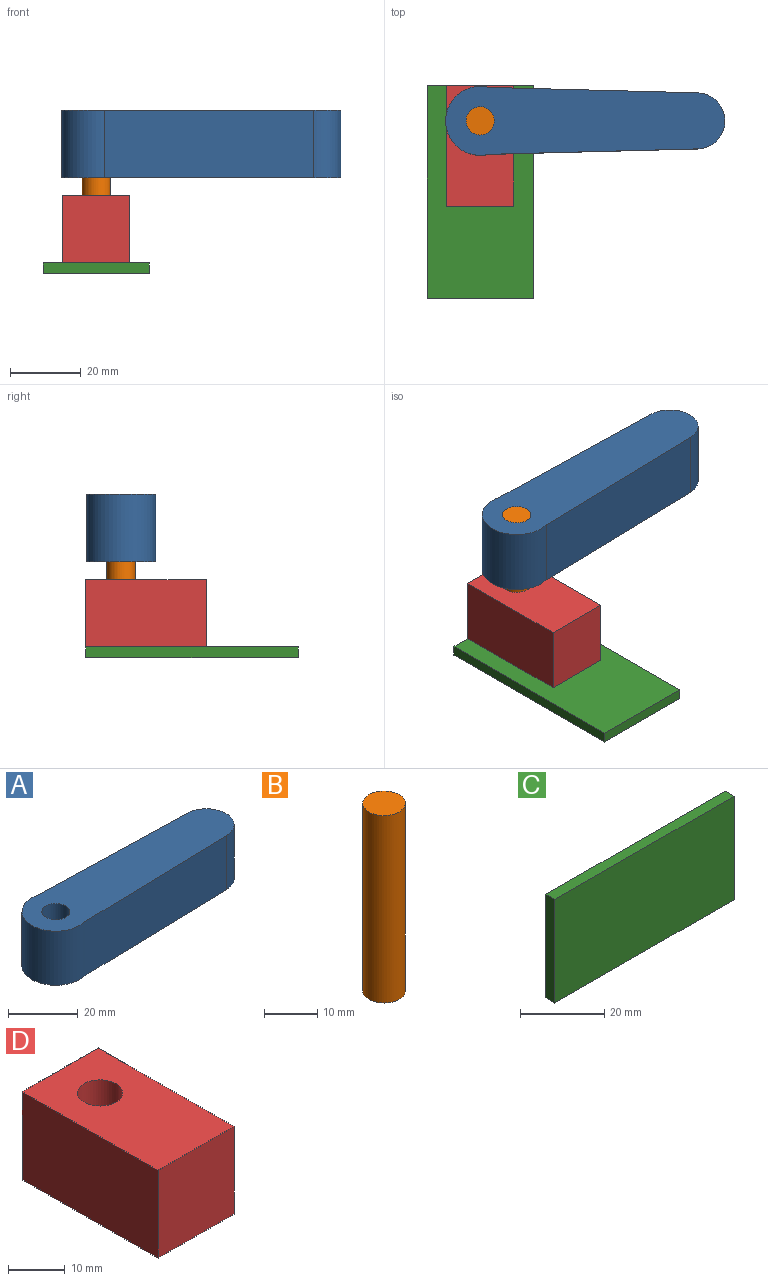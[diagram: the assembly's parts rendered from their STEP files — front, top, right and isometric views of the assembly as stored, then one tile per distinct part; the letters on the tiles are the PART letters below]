
ASSEMBLY  parts=4 mates=3
PART A: 7 faces, bbox 78.8x19.5x19 mm
  f0: cylinder r=7.91mm len=19mm, axis (0,0,-1), area 464.2mm2, adj f1,f3,f5,f6
  f1: plane 58.96x19mm, normal (0.03,1,0), area 1120.6mm2, adj f0,f2,f5,f6
  f2: cylinder r=9.73mm len=19.46mm, axis (0,0,-1), area 671.6mm2, adj f1,f3,f5,f6
  f3: plane 58.96x19mm, normal (0.03,-1,0), area 1120.6mm2, adj f0,f2,f5,f6
  f4: cylinder r=4mm len=19mm, axis (0,0,-1), area 477.5mm2, adj f5,f6
  f5: plane 78.75x19.46mm, normal (0,0,1), area 1261.5mm2, adj f0,f1,f2,f3,f4
  f6: plane 78.75x19.46mm, normal (0,0,-1), area 1261.5mm2, adj f0,f1,f2,f3,f4
PART B: 3 faces, bbox 8x8x43 mm
  f0: cylinder r=4mm len=43mm, axis (0,0,-1), area 1080.7mm2, adj f1,f2
  f1: plane 8x8mm, normal (0,0,1), area 50.3mm2, adj f0
  f2: plane 8x8mm, normal (0,0,-1), area 50.3mm2, adj f0
PART C: 6 faces, bbox 60x3x30 mm
  f0: plane 60x3mm, normal (0,0,1), area 180mm2, adj f1,f3,f4,f5
  f1: plane 30x3mm, normal (-1,0,0), area 90mm2, adj f0,f2,f4,f5
  f2: plane 60x3mm, normal (0,0,-1), area 180mm2, adj f1,f3,f4,f5
  f3: plane 30x3mm, normal (1,0,0), area 90mm2, adj f0,f2,f4,f5
  f4: plane 60x30mm, normal (0,-1,0), area 1800mm2, adj f0,f1,f2,f3
  f5: plane 60x30mm, normal (0,1,0), area 1800mm2, adj f0,f1,f2,f3
PART D: 7 faces, bbox 19x34x19 mm
  f0: plane 19x19mm, normal (0,1,0), area 361mm2, adj f1,f3,f4,f5
  f1: plane 34x19mm, normal (-1,0,0), area 646mm2, adj f0,f2,f4,f5
  f2: plane 19x19mm, normal (0,-1,0), area 361mm2, adj f1,f3,f4,f5
  f3: plane 34x19mm, normal (1,0,0), area 646mm2, adj f0,f2,f4,f5
  f4: plane 34x19mm, normal (0,0,1), area 595.7mm2, adj f0,f1,f2,f3,f6
  f5: plane 34x19mm, normal (0,0,-1), area 595.7mm2, adj f0,f1,f2,f3,f6
  f6: cylinder r=4mm len=19mm, axis (0,0,1), area 477.5mm2, adj f4,f5
PLACE A t=(28.59,16.86,-8.19)mm
PLACE B rot(axis=(1,0,0),0deg) t=(-1.97,16.86,-32.19)mm
PLACE C rot(axis=(-0.58,0.58,-0.58),120deg) t=(-1.97,-3.14,-35.19)mm
PLACE D rot(axis=(0,1,0),180deg) t=(-1.97,9.86,-13.19)mm
MATE fastened D.f4 <-> C.f4  axis (0,0,-1) through (-1.97,26.86,-32.19)mm
MATE fastened B.f0 <-> A.f2  axis (0,0,1) through (-1.97,16.86,10.81)mm
MATE fastened B.f0 <-> D.f6  axis (0,0,-1) through (-1.97,16.86,-32.19)mm
